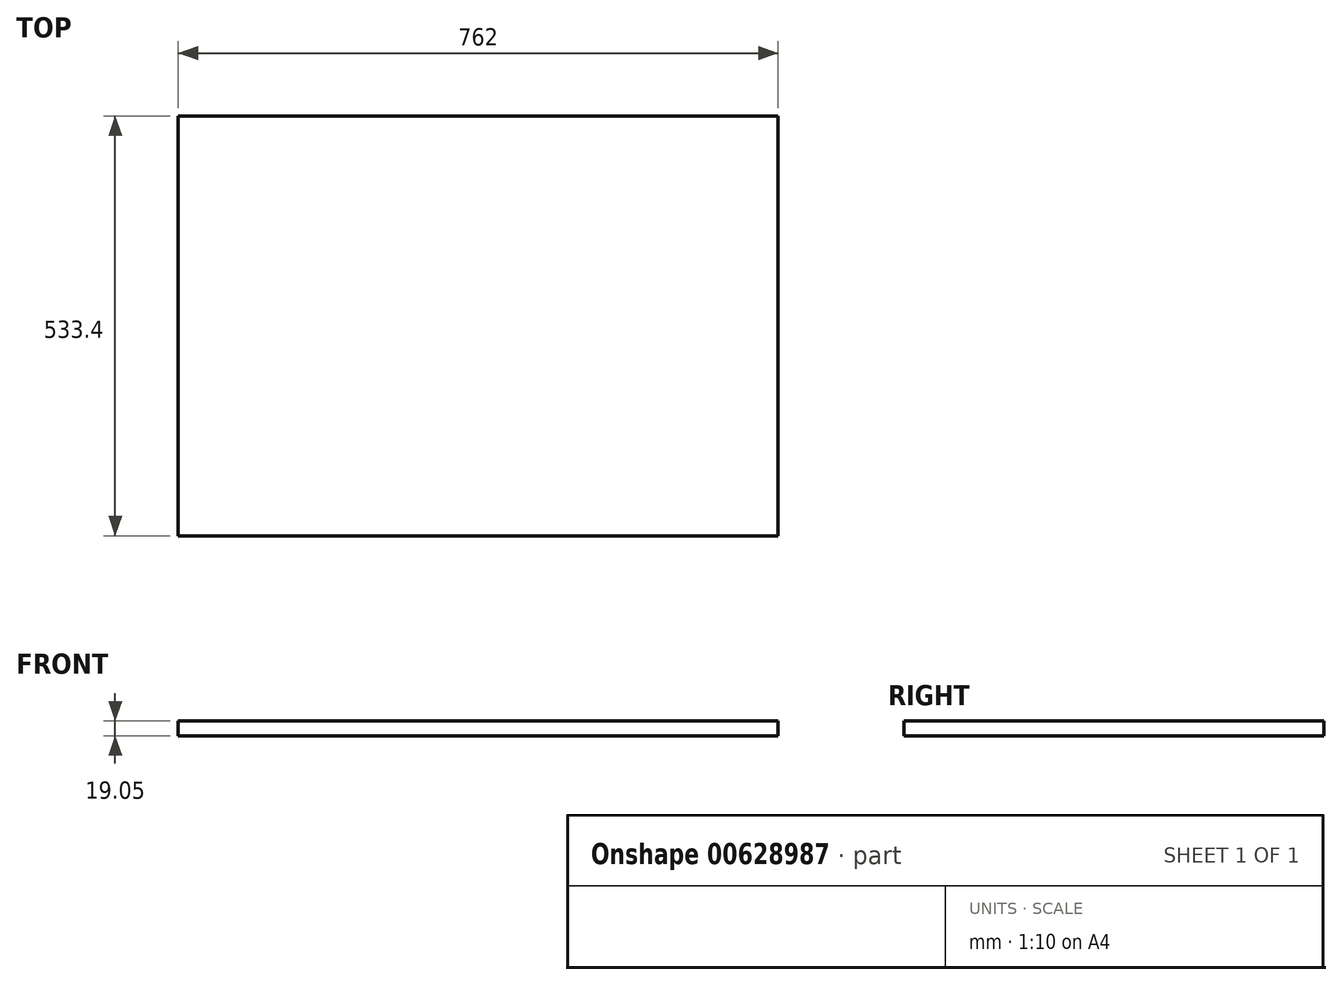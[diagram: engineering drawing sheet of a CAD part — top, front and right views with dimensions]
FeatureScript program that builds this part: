
annotation { "Feature Type Name" : "Feature", "Feature Type Description" : "" }
export const myFeature = defineFeature(function(context is Context, id is Id, definition is map)
    precondition{}
    {
        {
            var Q0;
            Q0=qCreatedBy(makeId("Top.planeOp"),FACE);
            var sketch = newSketch(context, id + "F0", { "sketchPlane" : qUnion([Q0])});
            skLineSegment(sketch, "E0.bottom", {"start": v(-381, 266.7) * mm, "end": v(381, 266.7) * mm});
            skLineSegment(sketch, "E0.top", {"start": v(-381, -266.7) * mm, "end": v(381, -266.7) * mm});
            skLineSegment(sketch, "E0.left", {"start": v(-381, 266.7) * mm, "end": v(-381, -266.7) * mm});
            skLineSegment(sketch, "E0.right", {"start": v(381, 266.7) * mm, "end": v(381, -266.7) * mm});
            skPoint(sketch, "E0.middle", {"position": v(0, 0) * mm});
            skSolve(sketch);
        }
        {
            var Q0;
            Q0=makeQuery(id+"F0.imprint","IMPRINT",FACE,{"disambiguationData":[TD([[makeQuery(id+"F0.imprint","IMPRINT",EDGE,{"derivedFrom":sQuery(id+"F0.wireOp",EDGE,"E0.bottom")}),-1.0]])]});
            extrude(context, id + "F1", {"entities" : qUnion([Q0]), "depth" : 19.05 * mm, "offsetDistance" : 25.4 * mm});
        }
    });
